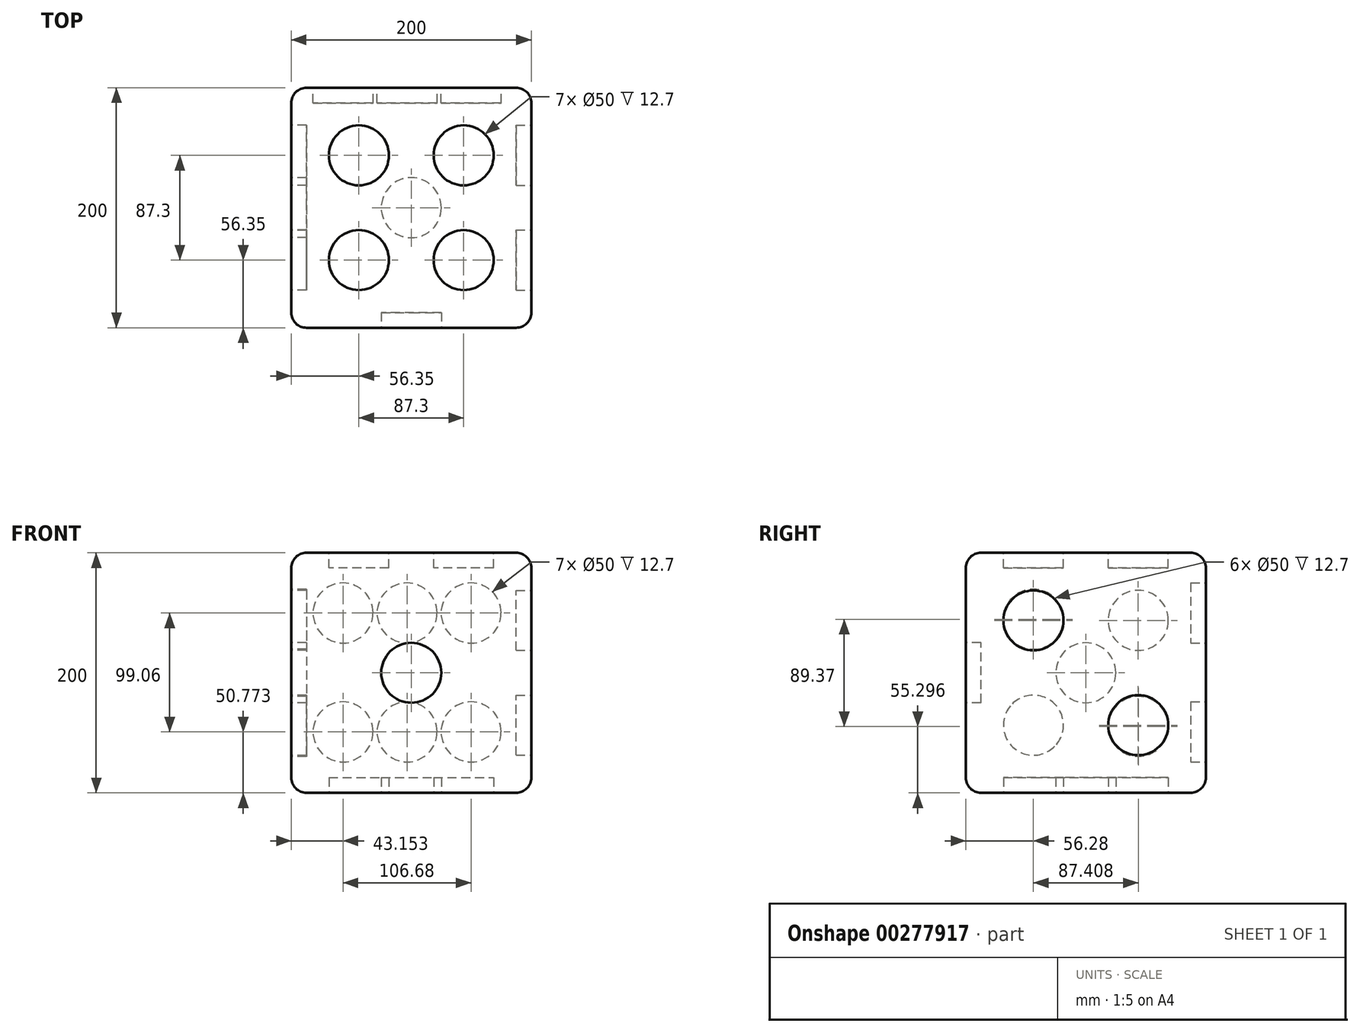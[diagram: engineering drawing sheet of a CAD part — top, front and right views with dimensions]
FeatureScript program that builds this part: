
annotation { "Feature Type Name" : "Feature", "Feature Type Description" : "" }
export const myFeature = defineFeature(function(context is Context, id is Id, definition is map)
    precondition{}
    {
        {
            var Q0;
            Q0=qCreatedBy(makeId("Top.planeOp"),FACE);
            var sketch = newSketch(context, id + "F0", { "sketchPlane" : qUnion([Q0])});
            skLineSegment(sketch, "E0.bottom", {"start": v(100, 100) * mm, "end": v(-100, 100) * mm});
            skLineSegment(sketch, "E0.top", {"start": v(100, -100) * mm, "end": v(-100, -100) * mm});
            skLineSegment(sketch, "E0.left", {"start": v(100, 100) * mm, "end": v(100, -100) * mm});
            skLineSegment(sketch, "E0.right", {"start": v(-100, 100) * mm, "end": v(-100, -100) * mm});
            skPoint(sketch, "E0.middle", {"position": v(0, 0) * mm});
            skSolve(sketch);
        }
        {
            var Q0;
            Q0=makeQuery(id+"F0.imprint","IMPRINT",FACE,{"disambiguationData":[TD([[makeQuery(id+"F0.imprint","IMPRINT",EDGE,{"derivedFrom":sQuery(id+"F0.wireOp",EDGE,"E0.bottom")}),1.0]])]});
            extrude(context, id + "F1", {"entities" : qUnion([Q0]), "depth" : 100 * mm, "hasSecondDirection" : true, "secondDirectionOppositeDirection" : true, "secondDirectionDepth" : 100 * mm});
        }
        {
            var Q0;
            Q0=makeQuery(id+"F1.opExtrude","CAP_FACE",FACE,{"disambiguationData":[OSD([sQuery(id+"F0.wireOp",EDGE,"E0.bottom"),sQuery(id+"F0.wireOp",EDGE,"E0.top"),sQuery(id+"F0.wireOp",EDGE,"E0.left"),sQuery(id+"F0.wireOp",EDGE,"E0.right")])],"isStart":false});
            var Q1;
            Q1=makeQuery(id+"F1.opExtrude","SWEPT_FACE",FACE,{"disambiguationData":[OSD([sQuery(id+"F0.wireOp",EDGE,"E0.right")])]});
            var Q2;
            Q2=makeQuery(id+"F1.opExtrude","CAP_FACE",FACE,{"disambiguationData":[OSD([sQuery(id+"F0.wireOp",EDGE,"E0.bottom"),sQuery(id+"F0.wireOp",EDGE,"E0.top"),sQuery(id+"F0.wireOp",EDGE,"E0.left"),sQuery(id+"F0.wireOp",EDGE,"E0.right")])],"isStart":true});
            var Q3;
            Q3=makeQuery(id+"F1.opExtrude","SWEPT_FACE",FACE,{"disambiguationData":[OSD([sQuery(id+"F0.wireOp",EDGE,"E0.bottom")])]});
            var Q4;
            Q4=makeQuery(id+"F1.opExtrude","SWEPT_FACE",FACE,{"disambiguationData":[OSD([sQuery(id+"F0.wireOp",EDGE,"E0.top")])]});
            var Q5;
            Q5=makeQuery(id+"F1.opExtrude","SWEPT_FACE",FACE,{"disambiguationData":[OSD([sQuery(id+"F0.wireOp",EDGE,"E0.left")])]});
            fillet(context, id + "F2", {"entities" : qUnion([Q0, Q1, Q2, Q3, Q4, Q5]), "radius" : 12.7 * mm, "tangentPropagation" : true, "allowEdgeOverflow" : false});
        }
        {
            var Q0;
            Q0=makeQuery(id+"F1.opExtrude","SWEPT_FACE",FACE,{"disambiguationData":[OSD([sQuery(id+"F0.wireOp",EDGE,"E0.top")])]});
            var sketch = newSketch(context, id + "F3", { "sketchPlane" : qUnion([Q0])});
            skCircle(sketch, "E1", {"center": v(0, 0) * mm, "radius": 25 * mm});
            skSolve(sketch);
        }
        {
            var Q0;
            Q0=makeQuery(id+"F3.imprint","IMPRINT",FACE,{"disambiguationData":[TD([[makeQuery(id+"F3.imprint","IMPRINT",EDGE,{"derivedFrom":sQuery(id+"F3.wireOp",EDGE,"E1")}),1.0]])]});
            extrude(context, id + "F4", {"entities" : qUnion([Q0]), "operationType" : NewBodyOperationType.REMOVE, "oppositeDirection" : true, "depth" : 12.7 * mm});
        }
        {
            var Q0;
            Q0=makeQuery(id+"F1.opExtrude","SWEPT_FACE",FACE,{"disambiguationData":[OSD([sQuery(id+"F0.wireOp",EDGE,"E0.bottom")])]});
            var sketch = newSketch(context, id + "F5", { "sketchPlane" : qUnion([Q0])});
            skLineSegment(sketch, "E2", {"start": v(-87.3, 87.3) * mm, "end": v(0, 0) * mm, "construction": true});
            skLineSegment(sketch, "E3", {"start": v(0, 0) * mm, "end": v(-87.3, -87.3) * mm, "construction": true});
            skCircle(sketch, "E4", {"center": v(-49.83, 49.83) * mm, "radius": 25 * mm});
            skCircle(sketch, "E5.0.1.0", {"center": v(-49.83, -49.23) * mm, "radius": 25 * mm});
            skCircle(sketch, "E5.1.0.0", {"center": v(3.5, 49.83) * mm, "radius": 25 * mm});
            skCircle(sketch, "E5.1.1.0", {"center": v(3.5, -49.23) * mm, "radius": 25 * mm});
            skCircle(sketch, "E5.2.0.0", {"center": v(56.85, 49.83) * mm, "radius": 25 * mm});
            skCircle(sketch, "E5.2.1.0", {"center": v(56.85, -49.23) * mm, "radius": 25 * mm});
            skLineSegment(sketch, "E5.direction1", {"start": v(-49.83, 49.83) * mm, "end": v(3.5, 49.83) * mm, "construction": true});
            skLineSegment(sketch, "E5.direction2", {"start": v(-49.83, 49.83) * mm, "end": v(-49.83, -49.23) * mm, "construction": true});
            skSolve(sketch);
        }
        {
            var Q0;
            Q0=makeQuery(id+"F5.imprint","IMPRINT",FACE,{"disambiguationData":[TD([[makeQuery(id+"F5.imprint","IMPRINT",EDGE,{"derivedFrom":sQuery(id+"F5.wireOp",EDGE,"E4")}),1.0]])]});
            var Q1;
            Q1=makeQuery(id+"F5.imprint","IMPRINT",FACE,{"disambiguationData":[TD([[makeQuery(id+"F5.imprint","IMPRINT",EDGE,{"derivedFrom":sQuery(id+"F5.wireOp",EDGE,"E5.1.0.0")}),1.0]])]});
            var Q2;
            Q2=makeQuery(id+"F5.imprint","IMPRINT",FACE,{"disambiguationData":[TD([[makeQuery(id+"F5.imprint","IMPRINT",EDGE,{"derivedFrom":sQuery(id+"F5.wireOp",EDGE,"E5.2.0.0")}),1.0]])]});
            var Q3;
            Q3=makeQuery(id+"F5.imprint","IMPRINT",FACE,{"disambiguationData":[TD([[makeQuery(id+"F5.imprint","IMPRINT",EDGE,{"derivedFrom":sQuery(id+"F5.wireOp",EDGE,"E5.0.1.0")}),1.0]])]});
            var Q4;
            Q4=makeQuery(id+"F5.imprint","IMPRINT",FACE,{"disambiguationData":[TD([[makeQuery(id+"F5.imprint","IMPRINT",EDGE,{"derivedFrom":sQuery(id+"F5.wireOp",EDGE,"E5.1.1.0")}),1.0]])]});
            var Q5;
            Q5=makeQuery(id+"F5.imprint","IMPRINT",FACE,{"disambiguationData":[TD([[makeQuery(id+"F5.imprint","IMPRINT",EDGE,{"derivedFrom":sQuery(id+"F5.wireOp",EDGE,"E5.2.1.0")}),1.0]])]});
            extrude(context, id + "F6", {"entities" : qUnion([Q0, Q1, Q2, Q3, Q4, Q5]), "operationType" : NewBodyOperationType.REMOVE, "oppositeDirection" : true, "depth" : 12.7 * mm});
        }
        {
            var Q0;
            Q0=makeQuery(id+"F1.opExtrude","SWEPT_FACE",FACE,{"disambiguationData":[OSD([sQuery(id+"F0.wireOp",EDGE,"E0.right")])]});
            var sketch = newSketch(context, id + "F7", { "sketchPlane" : qUnion([Q0])});
            skLineSegment(sketch, "E6", {"start": v(-87.3, 87.3) * mm, "end": v(0, 0) * mm, "construction": true});
            skLineSegment(sketch, "E7", {"start": v(0, 0) * mm, "end": v(87.3, -87.3) * mm, "construction": true});
            skCircle(sketch, "E8", {"center": v(-43.65, 43.65) * mm, "radius": 25 * mm});
            skCircle(sketch, "E9", {"center": v(43.65, -43.65) * mm, "radius": 25 * mm});
            skCircle(sketch, "E10.0.1.0", {"center": v(-43.69, -44.7) * mm, "radius": 25 * mm});
            skCircle(sketch, "E10.1.0.0", {"center": v(43.72, 44.67) * mm, "radius": 25 * mm});
            skCircle(sketch, "E10.1.1.0", {"center": v(43.68, -43.69) * mm, "radius": 25 * mm});
            skLineSegment(sketch, "E10.direction1", {"start": v(-43.65, 43.65) * mm, "end": v(43.72, 44.67) * mm, "construction": true});
            skLineSegment(sketch, "E10.direction2", {"start": v(-43.65, 43.65) * mm, "end": v(-43.69, -44.7) * mm, "construction": true});
            skCircle(sketch, "E11", {"center": v(0, 0) * mm, "radius": 25 * mm});
            skSolve(sketch);
        }
        {
            var Q0;
            Q0=makeQuery(id+"F1.opExtrude","SWEPT_FACE",FACE,{"disambiguationData":[OSD([sQuery(id+"F0.wireOp",EDGE,"E0.left")])]});
            var sketch = newSketch(context, id + "F8", { "sketchPlane" : qUnion([Q0])});
            skSolve(sketch);
        }
        {
            var Q0;
            Q0 = qSketchRegion(id + "F7", true);
            extrude(context, id + "F9", {"entities" : qUnion([Q0]), "operationType" : NewBodyOperationType.REMOVE, "oppositeDirection" : true, "depth" : 12.7 * mm});
        }
        {
            var Q0;
            Q0=makeQuery(id+"F1.opExtrude","CAP_FACE",FACE,{"disambiguationData":[OSD([sQuery(id+"F0.wireOp",EDGE,"E0.bottom"),sQuery(id+"F0.wireOp",EDGE,"E0.top"),sQuery(id+"F0.wireOp",EDGE,"E0.left"),sQuery(id+"F0.wireOp",EDGE,"E0.right")])],"isStart":true});
            var sketch = newSketch(context, id + "F10", { "sketchPlane" : qUnion([Q0])});
            skLineSegment(sketch, "E12", {"start": v(87.3, 87.3) * mm, "end": v(0, 0) * mm, "construction": true});
            skLineSegment(sketch, "E13", {"start": v(0, 0) * mm, "end": v(-87.3, -87.3) * mm, "construction": true});
            skCircle(sketch, "E14", {"center": v(43.65, 43.65) * mm, "radius": 25 * mm});
            skCircle(sketch, "E15", {"center": v(0, 0) * mm, "radius": 25 * mm});
            skCircle(sketch, "E16", {"center": v(-43.65, -43.65) * mm, "radius": 25 * mm});
            skSolve(sketch);
        }
        {
            var Q0;
            Q0 = qSketchRegion(id + "F10", true);
            extrude(context, id + "F11", {"entities" : qUnion([Q0]), "operationType" : NewBodyOperationType.REMOVE, "oppositeDirection" : true, "depth" : 12.7 * mm});
        }
        {
            var Q0;
            Q0=makeQuery(id+"F1.opExtrude","CAP_FACE",FACE,{"disambiguationData":[OSD([sQuery(id+"F0.wireOp",EDGE,"E0.bottom"),sQuery(id+"F0.wireOp",EDGE,"E0.top"),sQuery(id+"F0.wireOp",EDGE,"E0.left"),sQuery(id+"F0.wireOp",EDGE,"E0.right")])],"isStart":false});
            var sketch = newSketch(context, id + "F12", { "sketchPlane" : qUnion([Q0])});
            skLineSegment(sketch, "E17", {"start": v(-87.3, 87.3) * mm, "end": v(0, 0) * mm, "construction": true});
            skLineSegment(sketch, "E18", {"start": v(0, 0) * mm, "end": v(87.3, 87.3) * mm, "construction": true});
            skLineSegment(sketch, "E19", {"start": v(0, 0) * mm, "end": v(87.3, -87.3) * mm, "construction": true});
            skLineSegment(sketch, "E20", {"start": v(0, 0) * mm, "end": v(-87.3, -87.3) * mm, "construction": true});
            skCircle(sketch, "E21", {"center": v(-43.65, 43.65) * mm, "radius": 25 * mm});
            skCircle(sketch, "E22", {"center": v(43.65, 43.65) * mm, "radius": 25 * mm});
            skCircle(sketch, "E23", {"center": v(43.65, -43.65) * mm, "radius": 25 * mm});
            skCircle(sketch, "E24", {"center": v(-43.65, -43.65) * mm, "radius": 25 * mm});
            skSolve(sketch);
        }
        {
            var Q0;
            Q0 = qSketchRegion(id + "F12", true);
            extrude(context, id + "F13", {"entities" : qUnion([Q0]), "operationType" : NewBodyOperationType.REMOVE, "oppositeDirection" : true, "depth" : 12.7 * mm});
        }
        {
            var Q0;
            {var subQ0=sQuery(id+"F0.wireOp",EDGE,"E0.left");var subQ1=makeQuery(id+"F1.opExtrude","SWEPT_FACE",FACE,{"disambiguationData":[OSD([subQ0])]});Q0=makeQuery(id+"F8.imprint","IMPRINT",FACE,{"disambiguationData":[TD([[makeQuery(id+"F8.imprint","IMPRINT",EDGE,{"derivedFrom":makeQuery(id+"F2.opFillet","BLEND_EDGE",EDGE,{"blendedFrom":[makeQuery(id+"F1.opExtrude","CAP_EDGE",EDGE,{"disambiguationData":[OSD([subQ0])],"isStart":true}),subQ1],"blendedInto":[subQ1]})}),1.0]])]});}
            var sketch = newSketch(context, id + "F14", { "sketchPlane" : qUnion([Q0])});
            skLineSegment(sketch, "E25.0", {"start": v(87.3, 87.3) * mm, "end": v(-87.3, 87.3) * mm, "construction": true});
            skLineSegment(sketch, "E26.0", {"start": v(-87.3, 87.3) * mm, "end": v(-87.3, -87.3) * mm, "construction": true});
            skLineSegment(sketch, "E27.0", {"start": v(-87.3, -87.3) * mm, "end": v(87.3, -87.3) * mm, "construction": true});
            skLineSegment(sketch, "E28.0", {"start": v(87.3, -87.3) * mm, "end": v(87.3, 87.3) * mm, "construction": true});
            skLineSegment(sketch, "E29", {"start": v(-87.3, 87.3) * mm, "end": v(0, 0) * mm, "construction": true});
            skLineSegment(sketch, "E30", {"start": v(0, 0) * mm, "end": v(87.3, -87.3) * mm, "construction": true});
            skCircle(sketch, "E31", {"center": v(-43.65, 43.65) * mm, "radius": 25 * mm});
            skCircle(sketch, "E32", {"center": v(43.65, -43.65) * mm, "radius": 25 * mm});
            skSolve(sketch);
        }
        {
            var Q0;
            Q0 = qSketchRegion(id + "F14", true);
            extrude(context, id + "F15", {"entities" : qUnion([Q0]), "operationType" : NewBodyOperationType.REMOVE, "oppositeDirection" : true, "depth" : 12.7 * mm});
        }
    });
